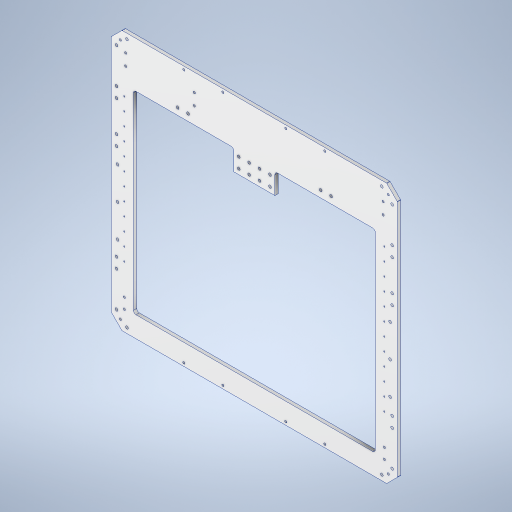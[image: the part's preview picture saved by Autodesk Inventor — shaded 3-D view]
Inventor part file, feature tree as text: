
AUTODESK INVENTOR PART (.ipt)
format: ipt  version: 2024 (Build 280153000, 153)  size: 791,552 bytes
history: native  units: mm
features: sketch x10, hole x6, extrude x4, projected_geometry x4, fillet x3, mirror x2
ambient origin geometry x8: Origin, YZ Plane, XZ Plane, XY Plane, X Axis, Y Axis, Z Axis, Center Point
bodies: Solid1 (feature_tree)
feature tree (29):
  extrude  "Extrusion1"  Depth=500.0mm
  hole  "Hole1"  [1 undecoded]
  extrude  "Extrusion4"  Depth=40.0mm
  extrude  "Extrusion5"  Depth=40.0mm
  hole  "Hole6"  [1 undecoded]
  hole  "Hole7"  [1 undecoded]
  mirror  "Mirror1"
  hole  "Hole8"  [1 undecoded]
  fillet  "Fillet2"  Radius=40.0mm
  fillet  "Fillet3"  Radius=20.0mm
  fillet  "Fillet4"  Radius=40.0mm
  extrude  "Extrusion6"  Depth=40.0mm
  hole  "Hole9"  [1 undecoded]
  hole  "Hole10"  [1 undecoded]
  mirror  "Mirror2"
  sketch  "Sketch1"  dims[d0=550.0mm d1=500.0mm]
  sketch  "Sketch2"  dims[d2=6.35mm d3=0.0mm d4=40.0mm]
  sketch  "Sketch9"  dims[d5=40.0mm d6=40.0mm]
  projected_geometry  "Projected Loop2"
  sketch  "Sketch10"  dims[d7=40.0mm d8=80.0mm]
  sketch  "Sketch11"  dims[d9=40.0mm d10=40.0mm]
  sketch  "Sketch12"  dims[d11=40.0mm d13=40.0mm]
  sketch  "Sketch13"  dims[d14=40.0mm d15=20.0mm d16=40.0mm d17=20.0mm d18=40.0mm]
  sketch  "Sketch14"  dims[d19=40.0mm d20=20.0mm]
  projected_geometry  "Projected Loop3"
  sketch  "Sketch15"  dims[d21=40.0mm d22=20.0mm]
  projected_geometry  "Projected Loop4"
  sketch  "Sketch16"  dims[d23=3.0mm d24=275.0mm d25=20.0mm d26=40.0mm d27=20.0mm d28=40.0mm d29=20.0mm d30=40.0mm d31=20.0mm d32=40.0mm d33=392.0mm d35=10.0mm d36=10.0mm d37=88.0mm d40=88.0mm d42=48.0mm d44=164.0mm d49=10.0mm d51=162.0mm d52=20.0mm d53=20.0mm d54=20.0mm d55=20.0mm d56=20.0mm d57=20.0mm d58=20.0mm d59=20.0mm d60=20.0mm d61=20.0mm d62=20.0mm d63=20.0mm d64=20.0mm d65=20.0mm d66=20.0mm d67=20.0mm d68=20.0mm d69=20.0mm d70=60.0mm d71=20.0mm d72=5.3mm d73=6.0mm d74=4.0mm d75=2.0mm d76=90.0deg d77=8.0mm d78=20.594885mm d79=10.0mm d87=80.0mm d148=465.0mm d150=40.0mm d151=79.2mm d152=40.0mm d153=13.0mm d154=0.0mm d155=0.0mm d156=20.0mm d157=20.0mm d158=0.0mm d159=0.0mm d160=125.0mm d161=2.0mm d162=4.0mm d163=5.3mm d164=6.0mm d165=6.5mm d166=11.0mm d167=90.0deg d168=15.0mm d169=20.594885mm d170=12.0mm d171=300.0mm d172=275.0mm d173=120.0mm d175=25.0mm d176=10.0mm d178=10.0mm d180=25.0mm d181=95.0mm d182=2.459mm d183=6.0mm d184=4.0mm d185=2.0mm d186=90.0deg d187=8.0mm d188=20.594885mm d189=22.0mm d190=34.0mm d191=27.5mm d192=132.0mm d193=20.0mm d194=25.0mm d195=38.0mm d196=4.134mm d197=10.0mm d198=4.0mm d199=2.0mm d200=90.0deg d201=8.0mm d202=20.594885mm d203=5.0mm d204=5.0mm d205=1.0mm d206=10.0mm d207=0.0mm d208=17.5mm d209=17.5mm d210=17.5mm d211=17.5mm d212=4.134mm d213=10.0mm d214=4.0mm d215=2.0mm d216=90.0deg d217=8.0mm d218=20.594885mm d227=75.0mm d228=75.0mm d229=6.0mm d230=196.0mm d231=4.134mm d232=10.0mm d233=9.5mm d234=5.0mm d235=90.0deg d236=8.0mm d237=20.594885mm]
  projected_geometry  "Projected Loop5"
note: 6 required parameter values undecoded (feature->parameter linkage not recoverable at this tier; creation-order binding heuristic only, values carry confidence <= 0.55)
